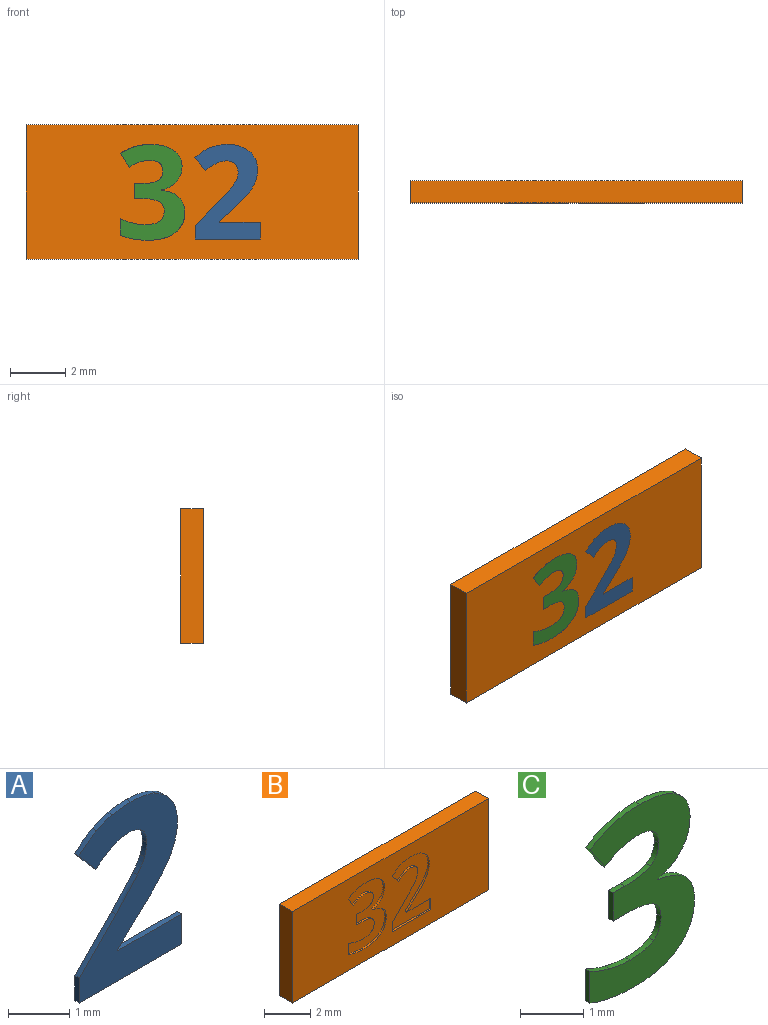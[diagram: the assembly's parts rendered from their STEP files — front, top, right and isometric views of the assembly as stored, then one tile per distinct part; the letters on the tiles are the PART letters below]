
ASSEMBLY  parts=3 mates=2
PART A: 26 faces, bbox 2.4x0.1x3.4 mm
  f0: plane 3.42x2.37mm, normal (0,-1,0), area 4.2mm2, adj f1,f2,f3,f4,f5,f6,f7,f8
  f1: plane 1.47x0.1mm, normal (0,0,1), area 0.1mm2, adj f0,f2,f22,f24
  f2: plane 0.1x0.03mm, normal (1,0,0), area 0mm2, adj f0,f1,f3,f22
  f3: plane 0.43x0.41mm, normal (0.69,0,-0.73), area 0.1mm2, adj f0,f2,f4,f22
  f4: extruded ~0.61x0.61mm, area 0.1mm2, adj f0,f3,f5,f22
  f5: extruded ~0.42x0.25mm, area 0mm2, adj f0,f4,f6,f22
  f6: extruded ~0.44x0.1mm, area 0mm2, adj f0,f5,f7,f22
  f7: extruded ~0.48x0.13mm, area 0.1mm2, adj f0,f6,f8,f22
  f8: extruded ~0.38x0.32mm, area 0.1mm2, adj f0,f7,f9,f22
  f9: extruded ~0.56x0.12mm, area 0.1mm2, adj f0,f8,f10,f22
  f10: extruded ~0.43x0.1mm, area 0mm2, adj f0,f9,f11,f22
  f11: extruded ~0.36x0.13mm, area 0mm2, adj f0,f10,f12,f22
  f12: extruded ~0.41x0.3mm, area 0.1mm2, adj f0,f11,f13,f22
  f13: plane 0.46x0.39mm, normal (-0.76,0,-0.65), area 0.1mm2, adj f0,f12,f14,f22
  f14: extruded ~0.39x0.26mm, area 0mm2, adj f0,f13,f15,f22
  f15: extruded ~0.38x0.1mm, area 0mm2, adj f0,f14,f16,f22
  f16: extruded ~0.3x0.1mm, area 0mm2, adj f0,f15,f17,f22
  f17: extruded ~0.3x0.11mm, area 0mm2, adj f0,f16,f18,f22
  f18: extruded ~0.26x0.1mm, area 0mm2, adj f0,f17,f19,f22
  f19: extruded ~0.28x0.17mm, area 0mm2, adj f0,f18,f20,f22
  f20: extruded ~0.53x0.49mm, area 0.1mm2, adj f0,f19,f21,f22
  f21: plane 0.86x0.85mm, normal (-0.71,0,0.7), area 0.1mm2, adj f0,f20,f22,f23
  f22: plane 3.42x2.37mm, normal (0,1,0), area 4.2mm2, adj f1,f2,f3,f4,f5,f6,f7,f8
  f23: plane 0.5x0.1mm, normal (-1,0,0), area 0mm2, adj f0,f21,f22,f25
  f24: plane 0.6x0.1mm, normal (1,0,0), area 0.1mm2, adj f0,f1,f22,f25
  f25: plane 2.36x0.1mm, normal (0,0,-1), area 0.2mm2, adj f0,f22,f23,f24
PART B: 59 faces, bbox 12x0.8x4.9 mm
  f0: plane 12x4.85mm, normal (0,-1,0), area 49.7mm2, adj f1,f2,f3,f4,f6,f7,f8,f9
  f1: plane 12x0.8mm, normal (0,0,-1), area 9.6mm2, adj f0,f2,f4,f5
  f2: plane 4.85x0.8mm, normal (1,0,0), area 3.9mm2, adj f0,f1,f3,f5
  f3: plane 12x0.8mm, normal (0,0,1), area 9.6mm2, adj f0,f2,f4,f5
  f4: plane 4.85x0.8mm, normal (-1,0,0), area 3.9mm2, adj f0,f1,f3,f5
  f5: plane 12x4.85mm, normal (0,1,0), area 58.2mm2, adj f1,f2,f3,f4
  f6: plane 0.6x0.1mm, normal (-1,0,0), area 0.1mm2, adj f0,f7,f29,f30
  f7: plane 1.47x0.1mm, normal (0,0,-1), area 0.1mm2, adj f0,f6,f8,f30
  f8: plane 0.1x0.03mm, normal (-1,0,0), area 0mm2, adj f0,f7,f9,f30
  f9: plane 0.43x0.41mm, normal (-0.69,0,0.73), area 0.1mm2, adj f0,f8,f10,f30
  f10: extruded ~0.61x0.61mm, area 0.1mm2, adj f0,f9,f11,f30
  f11: extruded ~0.42x0.25mm, area 0mm2, adj f0,f10,f12,f30
  f12: extruded ~0.44x0.1mm, area 0mm2, adj f0,f11,f13,f30
  f13: extruded ~0.48x0.13mm, area 0.1mm2, adj f0,f12,f14,f30
  f14: extruded ~0.38x0.32mm, area 0.1mm2, adj f0,f13,f15,f30
  f15: extruded ~0.56x0.12mm, area 0.1mm2, adj f0,f14,f16,f30
  f16: extruded ~0.43x0.1mm, area 0mm2, adj f0,f15,f17,f30
  f17: extruded ~0.36x0.13mm, area 0mm2, adj f0,f16,f18,f30
  f18: extruded ~0.41x0.3mm, area 0.1mm2, adj f0,f17,f19,f30
  f19: plane 0.46x0.39mm, normal (0.76,0,0.65), area 0.1mm2, adj f0,f18,f20,f30
  f20: extruded ~0.39x0.26mm, area 0mm2, adj f0,f19,f21,f30
  f21: extruded ~0.38x0.1mm, area 0mm2, adj f0,f20,f22,f30
  f22: extruded ~0.3x0.1mm, area 0mm2, adj f0,f21,f23,f30
  f23: extruded ~0.3x0.11mm, area 0mm2, adj f0,f22,f24,f30
  f24: extruded ~0.26x0.1mm, area 0mm2, adj f0,f23,f25,f30
  f25: extruded ~0.28x0.17mm, area 0mm2, adj f0,f24,f26,f30
  f26: extruded ~0.53x0.49mm, area 0.1mm2, adj f0,f25,f27,f30
  f27: plane 0.86x0.85mm, normal (0.71,0,-0.7), area 0.1mm2, adj f0,f26,f28,f30
  f28: plane 0.5x0.1mm, normal (1,0,0), area 0mm2, adj f0,f27,f29,f30
  f29: plane 2.36x0.1mm, normal (0,0,1), area 0.2mm2, adj f0,f6,f28,f30
  f30: plane 3.42x2.37mm, normal (0,-1,0), area 4.2mm2, adj f6,f7,f8,f9,f10,f11,f12,f13
  f31: extruded ~0.59x0.3mm, area 0.1mm2, adj f0,f32,f57,f58
  f32: extruded ~0.83x0.21mm, area 0.1mm2, adj f0,f31,f33,f58
  f33: extruded ~1.1x0.33mm, area 0.1mm2, adj f0,f32,f34,f58
  f34: plane 0.49x0.33mm, normal (0.83,0,0.56), area 0.1mm2, adj f0,f33,f35,f58
  f35: extruded ~0.38x0.19mm, area 0mm2, adj f0,f34,f36,f58
  f36: extruded ~0.34x0.1mm, area 0mm2, adj f0,f35,f37,f58
  f37: extruded ~0.48x0.38mm, area 0.1mm2, adj f0,f36,f38,f58
  f38: extruded ~0.35x0.18mm, area 0mm2, adj f0,f37,f39,f58
  f39: extruded ~0.57x0.1mm, area 0.1mm2, adj f0,f38,f40,f58
  f40: plane 0.26x0.1mm, normal (0,0,-1), area 0mm2, adj f0,f39,f41,f58
  f41: plane 0.55x0.1mm, normal (1,0,0), area 0.1mm2, adj f0,f40,f42,f58
  f42: plane 0.26x0.1mm, normal (0,0,1), area 0mm2, adj f0,f41,f43,f58
  f43: extruded ~0.62x0.1mm, area 0.1mm2, adj f0,f42,f44,f58
  f44: extruded ~0.34x0.19mm, area 0mm2, adj f0,f43,f45,f58
  f45: extruded ~0.39x0.17mm, area 0mm2, adj f0,f44,f46,f58
  f46: extruded ~0.52x0.12mm, area 0.1mm2, adj f0,f45,f47,f58
  f47: extruded ~0.47x0.1mm, area 0mm2, adj f0,f46,f48,f58
  f48: extruded ~0.43x0.16mm, area 0mm2, adj f0,f47,f49,f58
  f49: plane 0.61x0.1mm, normal (1,0,0), area 0.1mm2, adj f0,f48,f50,f58
  f50: extruded ~0.97x0.18mm, area 0.1mm2, adj f0,f49,f51,f58
  f51: extruded ~1.01x0.27mm, area 0.1mm2, adj f0,f50,f52,f58
  f52: extruded ~0.76x0.35mm, area 0.1mm2, adj f0,f51,f53,f58
  f53: extruded ~0.53x0.21mm, area 0.1mm2, adj f0,f52,f54,f58
  f54: extruded ~0.62x0.25mm, area 0.1mm2, adj f0,f53,f55,f58
  f55: plane 0.1x0.01mm, normal (-1,0,0), area 0mm2, adj f0,f54,f56,f58
  f56: extruded ~0.54x0.3mm, area 0.1mm2, adj f0,f55,f57,f58
  f57: extruded ~0.54x0.19mm, area 0.1mm2, adj f0,f31,f56,f58
  f58: plane 3.47x2.33mm, normal (0,-1,0), area 4.3mm2, adj f31,f32,f33,f34,f35,f36,f37,f38
PART C: 29 faces, bbox 2.3x0.1x3.5 mm
  f0: plane 3.47x2.33mm, normal (0,-1,0), area 4.3mm2, adj f1,f2,f3,f4,f5,f6,f7,f8
  f1: extruded ~0.83x0.21mm, area 0.1mm2, adj f0,f2,f25,f27
  f2: extruded ~1.1x0.33mm, area 0.1mm2, adj f0,f1,f3,f25
  f3: plane 0.49x0.33mm, normal (-0.83,0,-0.56), area 0.1mm2, adj f0,f2,f4,f25
  f4: extruded ~0.38x0.19mm, area 0mm2, adj f0,f3,f5,f25
  f5: extruded ~0.34x0.1mm, area 0mm2, adj f0,f4,f6,f25
  f6: extruded ~0.48x0.38mm, area 0.1mm2, adj f0,f5,f7,f25
  f7: extruded ~0.35x0.18mm, area 0mm2, adj f0,f6,f8,f25
  f8: extruded ~0.57x0.1mm, area 0.1mm2, adj f0,f7,f9,f25
  f9: plane 0.26x0.1mm, normal (0,0,1), area 0mm2, adj f0,f8,f10,f25
  f10: plane 0.55x0.1mm, normal (-1,0,0), area 0.1mm2, adj f0,f9,f11,f25
  f11: plane 0.26x0.1mm, normal (0,0,-1), area 0mm2, adj f0,f10,f12,f25
  f12: extruded ~0.62x0.1mm, area 0.1mm2, adj f0,f11,f13,f25
  f13: extruded ~0.34x0.19mm, area 0mm2, adj f0,f12,f14,f25
  f14: extruded ~0.39x0.17mm, area 0mm2, adj f0,f13,f15,f25
  f15: extruded ~0.52x0.12mm, area 0.1mm2, adj f0,f14,f16,f25
  f16: extruded ~0.47x0.1mm, area 0mm2, adj f0,f15,f17,f25
  f17: extruded ~0.43x0.16mm, area 0mm2, adj f0,f16,f18,f25
  f18: plane 0.61x0.1mm, normal (-1,0,0), area 0.1mm2, adj f0,f17,f19,f25
  f19: extruded ~0.97x0.18mm, area 0.1mm2, adj f0,f18,f20,f25
  f20: extruded ~1.01x0.27mm, area 0.1mm2, adj f0,f19,f21,f25
  f21: extruded ~0.76x0.35mm, area 0.1mm2, adj f0,f20,f22,f25
  f22: extruded ~0.53x0.21mm, area 0.1mm2, adj f0,f21,f23,f25
  f23: extruded ~0.62x0.25mm, area 0.1mm2, adj f0,f22,f24,f25
  f24: plane 0.1x0.01mm, normal (1,0,0), area 0mm2, adj f0,f23,f25,f26
  f25: plane 3.47x2.33mm, normal (0,1,0), area 4.3mm2, adj f1,f2,f3,f4,f5,f6,f7,f8
  f26: extruded ~0.54x0.3mm, area 0.1mm2, adj f0,f24,f25,f28
  f27: extruded ~0.59x0.3mm, area 0.1mm2, adj f0,f1,f25,f28
  f28: extruded ~0.54x0.19mm, area 0.1mm2, adj f0,f25,f26,f27
PLACE A t=(-0.18,0.4,-0.04)mm
PLACE B t=(0.04,0.4,-0.04)mm
PLACE C t=(-2.9,0.4,-0.04)mm
MATE fastened C.f0 <-> B.f0  axis (0,-1,0) through (-2.56,-0.4,-1.6)mm
MATE fastened A.f0 <-> B.f0  axis (0,-1,0) through (0.15,-0.4,-1.74)mm
